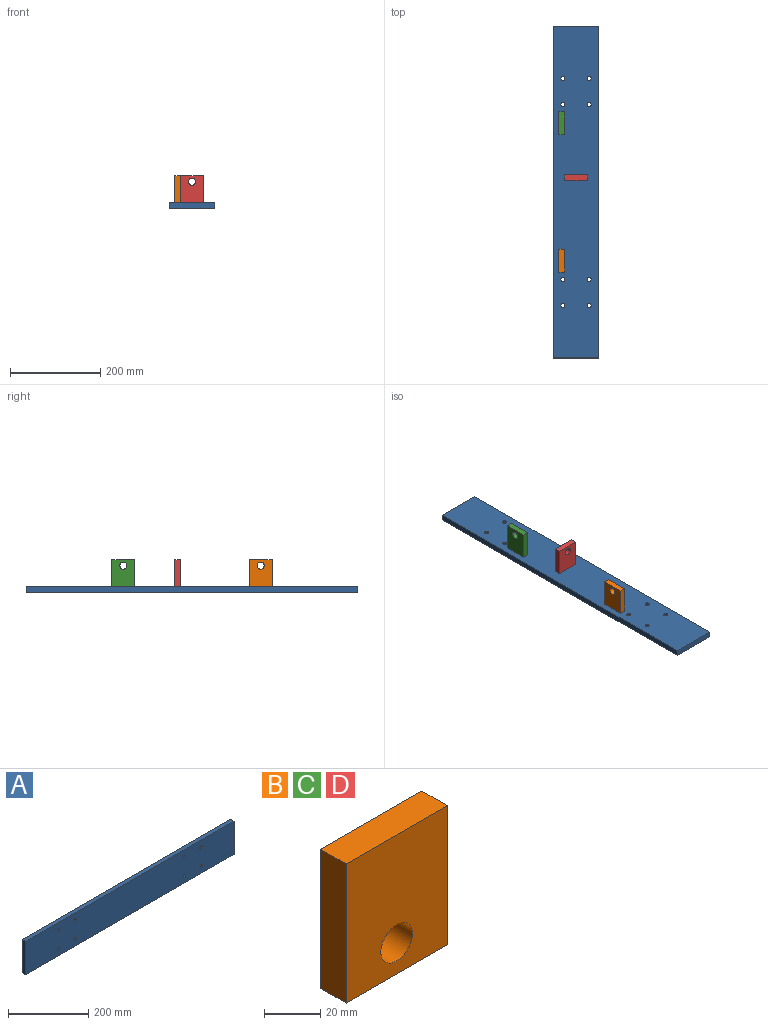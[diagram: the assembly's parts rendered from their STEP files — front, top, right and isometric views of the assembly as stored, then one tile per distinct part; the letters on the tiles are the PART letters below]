
ASSEMBLY  parts=4 mates=3
PART A: 14 faces, bbox 736.6x12.7x101.6 mm
  f0: plane 736.6x12.7mm, normal (0,0,1), area 9354.8mm2, adj f1,f3,f4,f5
  f1: plane 101.6x12.7mm, normal (-1,0,0), area 1290.3mm2, adj f0,f2,f4,f5
  f2: plane 736.6x12.7mm, normal (0,0,-1), area 9354.8mm2, adj f1,f3,f4,f5
  f3: plane 101.6x12.7mm, normal (1,0,0), area 1290.3mm2, adj f0,f2,f4,f5
  f4: plane 736.6x101.6mm, normal (0,-1,0), area 74330.6mm2, adj f0,f1,f2,f3,f6,f7,f8,f9
  f5: plane 736.6x101.6mm, normal (0,1,0), area 74330.6mm2, adj f0,f1,f2,f3,f6,f7,f8,f9
  f6: cylinder r=4.5mm len=12.7mm, axis (0,-1,0), area 358.7mm2, adj f4,f5
  f7: cylinder r=4.5mm len=12.7mm, axis (0,-1,0), area 358.7mm2, adj f4,f5
  f8: cylinder r=4.5mm len=12.7mm, axis (0,-1,0), area 358.7mm2, adj f4,f5
  f9: cylinder r=4.5mm len=12.7mm, axis (0,-1,0), area 358.7mm2, adj f4,f5
  f10: cylinder r=4.5mm len=12.7mm, axis (0,-1,0), area 358.7mm2, adj f4,f5
  f11: cylinder r=4.5mm len=12.7mm, axis (0,-1,0), area 358.7mm2, adj f4,f5
  f12: cylinder r=4.5mm len=12.7mm, axis (0,-1,0), area 358.7mm2, adj f4,f5
  f13: cylinder r=4.5mm len=12.7mm, axis (0,-1,0), area 358.7mm2, adj f4,f5
PART B: 7 faces, bbox 50.8x12.7x60.5 mm
  f0: plane 50.8x12.7mm, normal (0,0,1), area 645.2mm2, adj f1,f3,f4,f5
  f1: plane 60.52x12.7mm, normal (-1,0,0), area 768.5mm2, adj f0,f2,f4,f5
  f2: plane 50.8x12.7mm, normal (0,0,-1), area 645.2mm2, adj f1,f3,f4,f5
  f3: plane 60.52x12.7mm, normal (1,0,0), area 768.5mm2, adj f0,f2,f4,f5
  f4: plane 60.52x50.8mm, normal (0,-1,0), area 2876.3mm2, adj f0,f1,f2,f3,f6
  f5: plane 60.52x50.8mm, normal (0,1,0), area 2876.3mm2, adj f0,f1,f2,f3,f6
  f6: cylinder r=7.94mm len=15.88mm, axis (0,-1,0), area 633.4mm2, adj f4,f5
PART C: same geometry as B
PART D: same geometry as B
PLACE A rot(axis=(-0.58,-0.58,0.58),120deg) t=(-228.53,-197.24,-112.55)mm
PLACE B rot(axis=(0.71,0.71,0),180deg) t=(-253.93,-349.64,-70.64)mm
PLACE C rot(axis=(0.71,-0.71,0),180deg) t=(-266.63,-44.84,-70.64)mm
PLACE D rot(axis=(0,-1,0),180deg) t=(-228.53,-159.14,-70.64)mm
MATE slider D.f0 <-> A.f4  axis (0,0,-1) through (-228.53,-159.14,-99.85)mm
MATE slider B.f0 <-> A.f4  axis (0,0,-1) through (-266.63,-375.04,-99.85)mm
MATE slider C.f0 <-> A.f4  axis (0,0,-1) through (-266.63,-44.84,-99.85)mm
